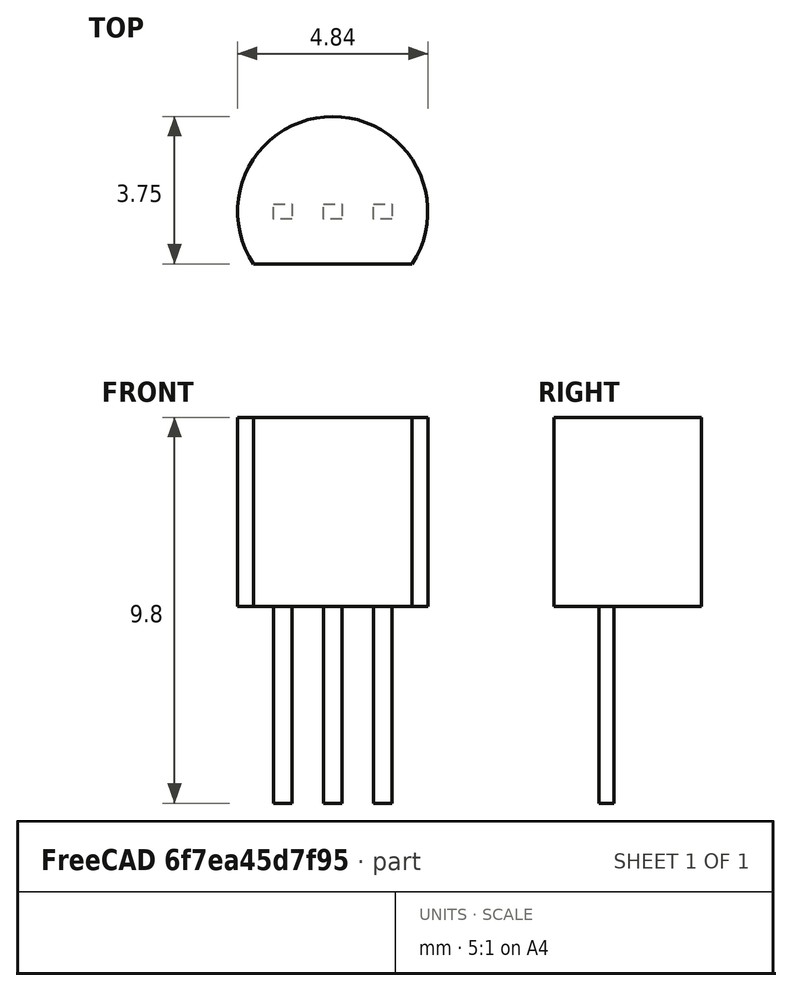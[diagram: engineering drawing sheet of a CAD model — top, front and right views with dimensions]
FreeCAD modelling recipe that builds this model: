
FCSTD DOCUMENT  (FreeCAD 0.17R13528 (Git))
Label: TO-92
License: All rights reserved
LicenseURL: http://en.wikipedia.org/wiki/All_rights_reserved
objects: Part::Part2DObjectPython×2, Part::Feature×1
note: 3 computed .brp shape members not serialized (recipe doc carries the construction recipe); baked Part::Feature solids carry a one-line shape summary decoded from their .brp

FEATURE [Part::Feature] Part__Feature  label="TO-92_Inline_Narrow"
  shape: bbox 4.83 x 3.745 x 9.8 mm, 19 faces (baked)
FEATURE [Part::Part2DObjectPython] ShapeString001  # Draft 2D object (typed FeaturePython)
  FontFile = <userpath>/Desktop/Freecad Projects/calibrib.ttf
  Placement = pos=(0,-1.34,4.5) rot=(1,0,0;1.5708rad)
  Size = 1
  String = 5088
  Support = -> [Part__Feature]
  Tracking = 0
FEATURE [Part::Part2DObjectPython] ShapeString  # Draft 2D object (typed FeaturePython)
  FontFile = <userpath>/Desktop/Freecad Projects/calibrib.ttf
  Placement = pos=(0,-1.34,5.5) rot=(1,0,0;1.5708rad)
  Size = 1
  String = 2N
  Support = -> [Part__Feature]
  Tracking = 0
